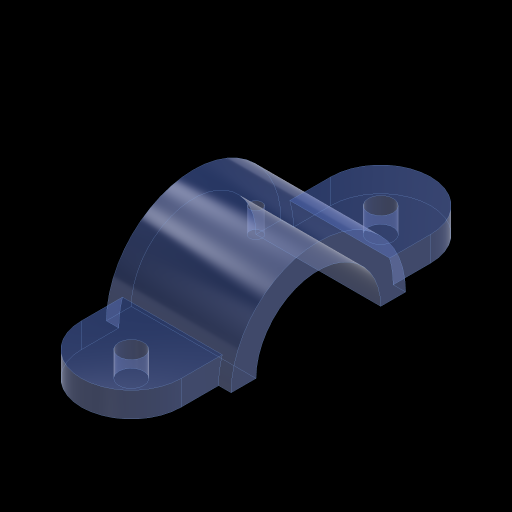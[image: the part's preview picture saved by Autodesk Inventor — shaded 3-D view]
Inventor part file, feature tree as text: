
AUTODESK INVENTOR PART (.ipt)
format: ipt  version: 2024 (Build 280153000, 153)  size: 164,864 bytes
history: native  units: in
note: dims shown in document units (in); Inventor stores cm internally (conversion verified against a paired STEP export)
features: extrude x4, sketch x3
ambient origin geometry x8: Origin, YZ Plane, XZ Plane, XY Plane, X Axis, Y Axis, Z Axis, Center Point
bodies: Solid1 (feature_tree)
feature tree (7):
  extrude  "BASE"  Depth=0.5in
  sketch  "Sketch2"  dims[d2=0.5in d3=1.0in]
  extrude  "REMOVED CENTER OF BASE"  Depth=1.0in
  extrude  "ARCH"  Depth=1.75in
  extrude  "TOPHOLE"  Depth=2.5in
  sketch  "Sketch1"  dims[d0=5.0in d1=0.5in]
  sketch  "Sketch3"  dims[d5=0.5in d6=0.0in d7=1.75in d8=1.25in d9=0.0in d10=0.0in d11=2.5in d12=0.0in d13=0.25in d14=0.0in d15=0.0in]
